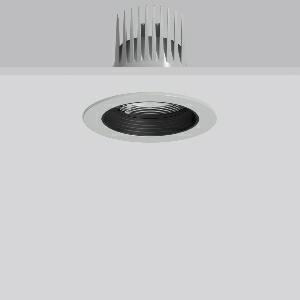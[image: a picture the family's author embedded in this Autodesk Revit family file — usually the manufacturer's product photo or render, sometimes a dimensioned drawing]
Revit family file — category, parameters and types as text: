
# Revit family: heledon_maxi_e_901789_004_2_76_e774
name_source: partatom
category: Lighting Fixtures
units: mm (PartAtom-declared; Revit-internal decimal feet)

## family parameters
Cut with Voids When Loaded = No
Host = Face
Light Source = No
Part Type = Normal
Room Calculation Point = No
Round Connector Dimension = Use Diameter
Shared = No

## types (1)
- HELEDON maxi E (1 x LED Modul 927 bakery, 2850 lm, 2700)
    Apparent Load = 33 VA
    Approval mark = CE
    CIE Flux Codes = 96 99 100 100 100
    Color Rendering = 90
    Color Temperature = 2700
    Default Elevation = 1800 mm
    Description = Series: HELEDON maxi
Round recessed downlight. Housing: die-cast aluminium, powder-coated. Black plastic ring and recessed LED to prevent glare from the side. Optical assembly with lens made of plastic (polycarbonate) for the best homogeneous light distribution - can be changed without tools. Special LED for illumination of pastries included. Suitable for Recessed ceiling mounting. Installation without tools thanks to spring fastening system. Including separate LED converter with connecting cable 600 mm.High quality converter without flickering and stroboscopic effect. Through-wiring box (5 pole) available as accessory. The following accessories can be mounted without use of tools: interchangeable lenses, decorative glasses, honeycomb louvre, clear and frosted diffusers, white interchangeable plastic ring. 
Colour: silver
Diameter: 162 mm
Height: 3 mm
Cut-out diameter: 152 mm
Recess height: 200 mm
Luminaire: recess height: 135 mm
Lamp: LED
Socket: without socket
Colour temperature: bakery
Colour rendering index (CRI): 97
System power: 33 W
Rated luminous flux: 2850 lm
Luminous efficiency: 86 lm/W
Control gear: Converter, dimmable, DALI
Protection class: II
Type of protection: IP 20
    Height = 0 mm  [stored 0 ft]
    Lamp = 1 x LED Modul 927 bakery
    Lamp Light Flux = 2850 lm
    Lamp count = 1
    Length = 162 mm
    Lifetime = 50000 h
    Luminous efficacy = 86 lm/W
    Manufacturer = RZB
    ModVariant = No
    Model = 901789.004.2.76
    Mounting Place = Ceiling
    Mounting Type = Recessed
    Number of Poles = 1
    OnlyDefault = Yes
    Power Factor = 1
    Product Name = HELEDON maxi E
    Product group = Recessed downlights
    ProductGroupID = 402
    Protection Class = Protection class II
    Protection Degree = IP 20
    RLX_Detail_Level = 1
    RLX_Emergency_Light_Flux = 0 lm
    RLX_Emergency_Type = 0
    RLX_Emergency_Type_DB = No
    RlxData = <blob elided: 119033 chars, md5=32705ff6>
    Socket = socket
    Standby Power = 0 W
    System Light Flux = 2850 lm
    System Power = 33 W
    Type Comments = Product without accessories
    Type Image = 901663.004.jpg
    URL = http://relux.com
    VarID = ---
    Voltage = 230 V
    Voltage Range = 220-240 V
    Weight = 0.00 kg
    Width = 0 mm  [stored 0 ft]

note: [stored X ft] marks values corroborated as IEEE doubles in the binary element streams (Revit-internal decimal feet)

## geometry (parser evidence)
native form markers: Blend x4, Sweep x10
no freeform markers — native parametric forms only
